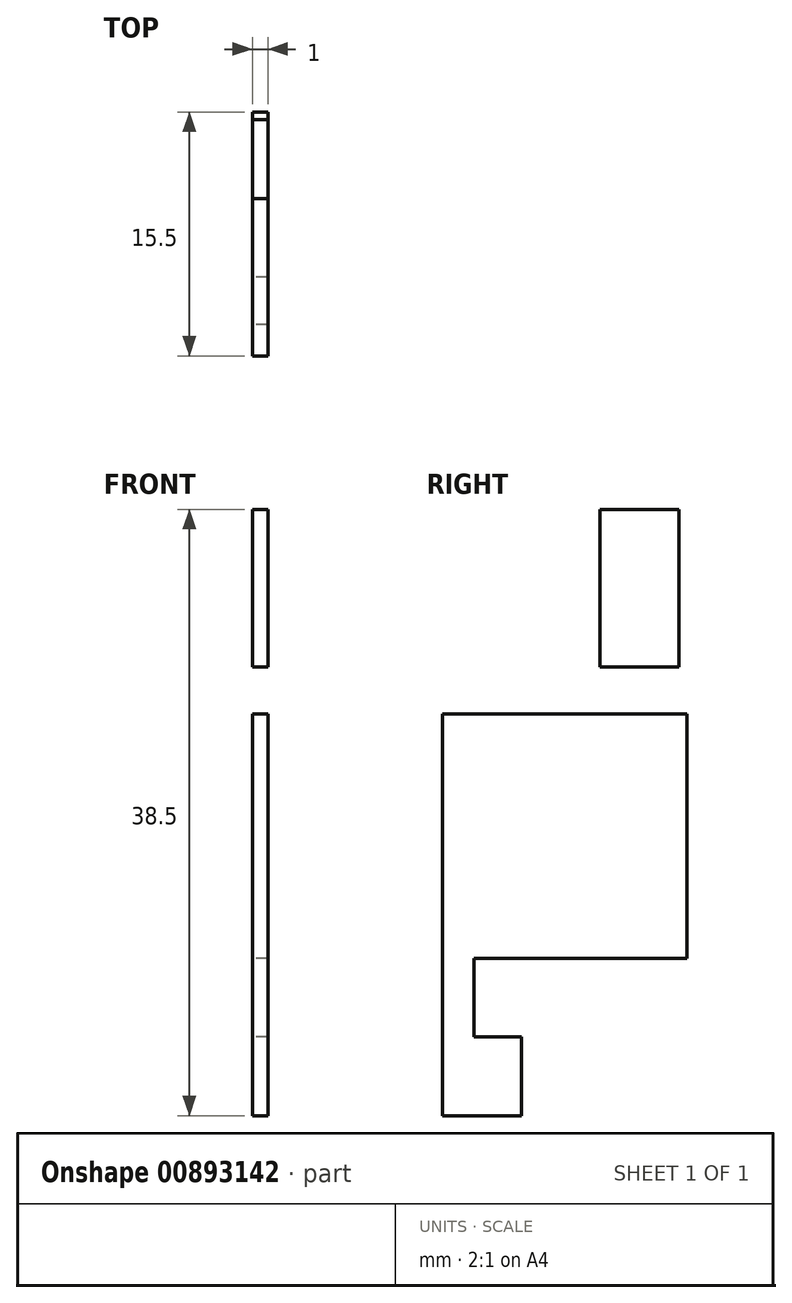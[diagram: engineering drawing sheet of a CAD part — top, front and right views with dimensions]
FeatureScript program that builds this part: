
annotation { "Feature Type Name" : "Feature", "Feature Type Description" : "" }
export const myFeature = defineFeature(function(context is Context, id is Id, definition is map)
    precondition{}
    {
        {
            var Q0;
            Q0=qCreatedBy(makeId("Right.planeOp"),FACE);
            var sketch = newSketch(context, id + "F0", { "sketchPlane" : qUnion([Q0])});
            skLineSegment(sketch, "E0.bottom", {"start": v(0, 0) * mm, "end": v(11.5, 0) * mm});
            skLineSegment(sketch, "E0.top", {"start": v(0, -15) * mm, "end": v(4.35, -15) * mm});
            skLineSegment(sketch, "E1.trimOffspring", {"start": v(7.15, -15) * mm, "end": v(11.5, -15) * mm});
            skLineSegment(sketch, "E2", {"start": v(12.38, 18) * mm, "end": v(9.14, 18) * mm});
            skLineSegment(sketch, "E3.0", {"start": v(-1.75, 0) * mm, "end": v(-1.75, -15) * mm});
            skLineSegment(sketch, "E4.0", {"start": v(13.25, 0) * mm, "end": v(13.25, -15) * mm});
            skLineSegment(sketch, "E5", {"start": v(-1.75, 0) * mm, "end": v(13.25, 0) * mm});
            skLineSegment(sketch, "E6", {"start": v(13.25, -15) * mm, "end": v(7.15, -15) * mm});
            skPoint(sketch, "E7.orphan", {"position": v(7.38, 18) * mm});
            skPoint(sketch, "E8.orphan", {"position": v(7.38, 3) * mm});
            skLineSegment(sketch, "E9", {"start": v(13.57, 18) * mm, "end": v(9.14, 18) * mm});
            skPoint(sketch, "E10.start.orphan", {"position": v(5.75, -15) * mm});
            skLineSegment(sketch, "E11", {"start": v(7.87, 18) * mm, "end": v(9.14, 18) * mm});
            skLineSegment(sketch, "E12", {"start": v(7.88, 13) * mm, "end": v(10.98, 13) * mm});
            skLineSegment(sketch, "E13.0", {"start": v(-3.75, 0) * mm, "end": v(-3.75, -15) * mm});
            skLineSegment(sketch, "E14.0", {"start": v(15.25, 0) * mm, "end": v(15.25, -15) * mm});
            skLineSegment(sketch, "E15", {"start": v(-2, 0) * mm, "end": v(13.5, 0) * mm});
            skLineSegment(sketch, "E16", {"start": v(-3.75, -15) * mm, "end": v(15.25, -15) * mm});
            skLineSegment(sketch, "E17.0", {"start": v(-3.75, -15.5) * mm, "end": v(15.25, -15.5) * mm});
            skLineSegment(sketch, "E18.0", {"start": v(-2, 0) * mm, "end": v(-2, -15) * mm});
            skLineSegment(sketch, "E19.0", {"start": v(13.5, 0) * mm, "end": v(13.5, -15) * mm});
            skLineSegment(sketch, "E20", {"start": v(-2, -15) * mm, "end": v(-2, -15.5) * mm});
            skLineSegment(sketch, "E21", {"start": v(13.5, -15) * mm, "end": v(13.5, -15.5) * mm});
            skLineSegment(sketch, "E22", {"start": v(10.98, 13) * mm, "end": v(6.98, 13) * mm});
            skLineSegment(sketch, "E23", {"start": v(6.98, 3) * mm, "end": v(10.98, 3) * mm});
            skLineSegment(sketch, "E24", {"start": v(11.38, 13) * mm, "end": v(10.98, 13) * mm});
            skLineSegment(sketch, "E25", {"start": v(11.38, 3) * mm, "end": v(10.98, 3) * mm});
            skLineSegment(sketch, "E26", {"start": v(11.88, 13) * mm, "end": v(11.38, 13) * mm});
            skLineSegment(sketch, "E27", {"start": v(11.88, 3) * mm, "end": v(11.38, 3) * mm});
            skLineSegment(sketch, "E28", {"start": v(6.98, 3) * mm, "end": v(6.88, 3) * mm});
            skLineSegment(sketch, "E29", {"start": v(6.98, 13) * mm, "end": v(6.88, 13) * mm});
            skLineSegment(sketch, "E30.0", {"start": v(13, 13) * mm, "end": v(13, 3) * mm});
            skLineSegment(sketch, "E31.0", {"start": v(8, 3) * mm, "end": v(8, 13) * mm});
            skLineSegment(sketch, "E32", {"start": v(13, 13) * mm, "end": v(8, 13) * mm});
            skLineSegment(sketch, "E33", {"start": v(13, 3) * mm, "end": v(8, 3) * mm});
            skLineSegment(sketch, "E34", {"start": v(-2, -15.5) * mm, "end": v(-2, -25.5) * mm});
            skLineSegment(sketch, "E35", {"start": v(-2, -25.5) * mm, "end": v(3, -25.5) * mm});
            skLineSegment(sketch, "E36", {"start": v(3, -25.5) * mm, "end": v(3, -20.5) * mm});
            skLineSegment(sketch, "E37", {"start": v(3, -20.5) * mm, "end": v(0, -20.5) * mm});
            skLineSegment(sketch, "E38", {"start": v(0, -20.5) * mm, "end": v(0, -15.5) * mm});
            skSolve(sketch);
        }
        {
            var Q0;
            Q0=makeQuery(id+"F0.imprint","IMPRINT",FACE,{"disambiguationData":[TD([[makeQuery(id+"F0.imprint","IMPRINT",EDGE,{"derivedFrom":sQuery(id+"F0.wireOp",EDGE,"E0.bottom")}),-1.0]])]});
            var Q1;
            Q1=makeQuery(id+"F0.imprint","IMPRINT",FACE,{"disambiguationData":[TD([[makeQuery(id+"F0.imprint","IMPRINT",EDGE,{"derivedFrom":sQuery(id+"F0.wireOp",EDGE,"qPRy3xUT-NRqM-xTn5-TbLo-p4iQvefC5ACk")}),-1.0]])]});
            var Q2;
            {var subQ3=sQuery(id+"F0.wireOp",EDGE,"63f1d356-c40f-4f39-ade3-4e022c9102be.0");Q2=makeQuery(id+"F0.imprint","IMPRINT",FACE,{"disambiguationData":[TD([[makeQuery(id+"F0.imprint","IMPRINT",EDGE,{"derivedFrom":subQ3}),1.0]])]});}
            var Q3;
            {var subQ0=sQuery(id+"F0.wireOp",EDGE,"5dc07093-3f57-4306-a93b-4e72212c7467.0");Q3=makeQuery(id+"F0.imprint","IMPRINT",FACE,{"disambiguationData":[TD([[makeQuery(id+"F0.imprint","IMPRINT",EDGE,{"derivedFrom":subQ0}),1.0]])]});}
            var Q4;
            {var subQ0=sQuery(id+"F0.wireOp",EDGE,"51NmYdBp-mA1z-wu9Q-53MT-rEDAkP0LJ8wn");Q4=makeQuery(id+"F0.imprint","IMPRINT",FACE,{"disambiguationData":[TD([[makeQuery(id+"F0.imprint","IMPRINT",EDGE,{"derivedFrom":subQ0}),-1.0]])]});}
            var Q5;
            {var subQ0=sQuery(id+"F0.wireOp",EDGE,"gVsyd78I-1lBY-GYfF-3Sc2-CoKCdImTYK3s");Q5=makeQuery(id+"F0.imprint","IMPRINT",FACE,{"disambiguationData":[TD([[makeQuery(id+"F0.imprint","IMPRINT",EDGE,{"derivedFrom":subQ0}),-1.0]])]});}
            var Q6;
            {var subQ3=sQuery(id+"F0.wireOp",EDGE,"SiENeyCx-ZrQ5-kKsV-lLu2-aJ1GO4VE4cTd");Q6=makeQuery(id+"F0.imprint","IMPRINT",FACE,{"disambiguationData":[TD([[makeQuery(id+"F0.imprint","IMPRINT",EDGE,{"derivedFrom":subQ3}),1.0]])]});}
            var Q7;
            {var subQ0=sQuery(id+"F0.wireOp",EDGE,"E3.0");Q7=makeQuery(id+"F0.imprint","IMPRINT",FACE,{"disambiguationData":[TD([[makeQuery(id+"F0.imprint","IMPRINT",EDGE,{"derivedFrom":subQ0}),-1.0]])]});}
            var Q8;
            {var subQ0=sQuery(id+"F0.wireOp",EDGE,"E4.0");Q8=makeQuery(id+"F0.imprint","IMPRINT",FACE,{"disambiguationData":[TD([[makeQuery(id+"F0.imprint","IMPRINT",EDGE,{"derivedFrom":subQ0}),1.0]])]});}
            var Q9;
            {var subQ2=sQuery(id+"F0.wireOp",EDGE,"1mKygX2L-qfZs-mII2-diun-zsKhjgC72kff");Q9=makeQuery(id+"F0.imprint","IMPRINT",FACE,{"disambiguationData":[TD([[makeQuery(id+"F0.imprint","IMPRINT",EDGE,{"derivedFrom":subQ2}),-1.0]])]});}
            var Q10;
            {var subQ0=sQuery(id+"F0.wireOp",EDGE,"zi8WKg8l-IywR-yDlg-Gw4f-iAsSbMJXHt8X");var subQ3=makeQuery(id+"F0.imprint","IMPRINT",VERTEX,{"disambiguationData":[OD(0.0)],"derivedFrom":subQ0});Q10=makeQuery(id+"F0.imprint","IMPRINT",FACE,{"disambiguationData":[TD([[makeQuery(id+"F0.imprint","IMPRINT",EDGE,{"disambiguationData":[TD([[subQ3,-1.0]])],"derivedFrom":subQ0}),1.0]])]});}
            var Q11;
            {var subQ0=sQuery(id+"F0.wireOp",EDGE,"E16");var subQ1=sQuery(id+"F0.wireOp",EDGE,"9c8eaf94-47ad-4e4a-b23c-c071626e9017.0");var subQ2=makeQuery(id+"F0.imprint","INTERSECT",VERTEX,{"derivedFrom":[subQ1,subQ0]});Q11=makeQuery(id+"F0.imprint","IMPRINT",FACE,{"disambiguationData":[TD([[makeQuery(id+"F0.imprint","IMPRINT",EDGE,{"disambiguationData":[TD([[subQ2,-1.0]])],"derivedFrom":subQ1}),1.0]])]});}
            var Q12;
            Q12=makeQuery(id+"F0.imprint","IMPRINT",FACE,{"disambiguationData":[TD([[makeQuery(id+"F0.imprint","IMPRINT",EDGE,{"derivedFrom":sQuery(id+"F0.wireOp",EDGE,"b8907b82-ca3a-4fe0-9ae4-8b5bafafc062.0")}),1.0]])]});
            var Q13;
            {var subQ3=sQuery(id+"F0.wireOp",EDGE,"E3.0");Q13=makeQuery(id+"F0.imprint","IMPRINT",FACE,{"disambiguationData":[TD([[makeQuery(id+"F0.imprint","IMPRINT",EDGE,{"derivedFrom":subQ3}),1.0]])]});}
            var Q14;
            {var subQ5=sQuery(id+"F0.wireOp",EDGE,"3820a88b-3abb-40db-8bfc-c48b148b7aa2.0");Q14=makeQuery(id+"F0.imprint","IMPRINT",FACE,{"disambiguationData":[TD([[makeQuery(id+"F0.imprint","IMPRINT",EDGE,{"derivedFrom":subQ5}),-1.0]])]});}
            var Q15;
            {var subQ0=sQuery(id+"F0.wireOp",EDGE,"e7f2dfaa-ca02-423d-a241-3264b2101ff0.0");Q15=makeQuery(id+"F0.imprint","IMPRINT",FACE,{"disambiguationData":[TD([[makeQuery(id+"F0.imprint","IMPRINT",EDGE,{"derivedFrom":subQ0}),1.0]])]});}
            var Q16;
            {var subQ0=sQuery(id+"F0.wireOp",EDGE,"f3faf3d2-6f8b-4572-bc8f-cff6e40356fd.0");var subQ1=sQuery(id+"F0.wireOp",EDGE,"9c8eaf94-47ad-4e4a-b23c-c071626e9017.0");var subQ2=makeQuery(id+"F0.imprint","INTERSECT",VERTEX,{"derivedFrom":[subQ1,subQ0]});Q16=makeQuery(id+"F0.imprint","IMPRINT",FACE,{"disambiguationData":[TD([[makeQuery(id+"F0.imprint","IMPRINT",EDGE,{"disambiguationData":[TD([[subQ2,1.0]])],"derivedFrom":subQ1}),1.0]])]});}
            var Q17;
            {var subQ7=sQuery(id+"F0.wireOp",EDGE,"E20");Q17=makeQuery(id+"F0.imprint","IMPRINT",FACE,{"disambiguationData":[TD([[makeQuery(id+"F0.imprint","IMPRINT",EDGE,{"derivedFrom":subQ7}),1.0]])]});}
            var Q18;
            {var subQ2=sQuery(id+"F0.wireOp",EDGE,"E21");Q18=makeQuery(id+"F0.imprint","IMPRINT",FACE,{"disambiguationData":[TD([[makeQuery(id+"F0.imprint","IMPRINT",EDGE,{"derivedFrom":subQ2}),-1.0]])]});}
            var Q19;
            {var subQ0=sQuery(id+"F0.wireOp",EDGE,"e1832ce9-9692-4c92-918f-52eea242351d.0");Q19=makeQuery(id+"F0.imprint","IMPRINT",FACE,{"disambiguationData":[TD([[makeQuery(id+"F0.imprint","IMPRINT",EDGE,{"derivedFrom":subQ0}),-1.0]])]});}
            var Q20;
            {var subQ0=sQuery(id+"F0.wireOp",EDGE,"04c29579-a2e5-4540-a143-d3ab26432ee8.0");Q20=makeQuery(id+"F0.imprint","IMPRINT",FACE,{"disambiguationData":[TD([[makeQuery(id+"F0.imprint","IMPRINT",EDGE,{"derivedFrom":subQ0}),-1.0]])]});}
            var Q21;
            {var subQ0=sQuery(id+"F0.wireOp",EDGE,"c4b32359-1725-4305-a7d0-088cad5a7380.0");Q21=makeQuery(id+"F0.imprint","IMPRINT",FACE,{"disambiguationData":[TD([[makeQuery(id+"F0.imprint","IMPRINT",EDGE,{"derivedFrom":subQ0}),1.0]])]});}
            var Q22;
            {var subQ0=sQuery(id+"F0.wireOp",EDGE,"04c29579-a2e5-4540-a143-d3ab26432ee8.0");Q22=makeQuery(id+"F0.imprint","IMPRINT",FACE,{"disambiguationData":[TD([[makeQuery(id+"F0.imprint","IMPRINT",EDGE,{"derivedFrom":subQ0}),1.0]])]});}
            var Q23;
            {var subQ5=sQuery(id+"F0.wireOp",EDGE,"a76b719a-5e5b-4d65-aa66-56cd854adb41.trimOffspring");Q23=makeQuery(id+"F0.imprint","IMPRINT",FACE,{"disambiguationData":[TD([[makeQuery(id+"F0.imprint","IMPRINT",EDGE,{"derivedFrom":subQ5}),1.0]])]});}
            var Q24;
            {var subQ0=sQuery(id+"F0.wireOp",EDGE,"65d9d9e5-3152-4186-b4e5-152fd11331dc.0");var subQ1=sQuery(id+"F0.wireOp",EDGE,"E16");var subQ2=makeQuery(id+"F0.imprint","INTERSECT",VERTEX,{"derivedFrom":[subQ1,subQ0]});Q24=makeQuery(id+"F0.imprint","IMPRINT",FACE,{"disambiguationData":[TD([[makeQuery(id+"F0.imprint","IMPRINT",EDGE,{"disambiguationData":[TD([[subQ2,-1.0]])],"derivedFrom":subQ1}),-1.0]])]});}
            var Q25;
            {var subQ0=sQuery(id+"F0.wireOp",EDGE,"E16");var subQ1=sQuery(id+"F0.wireOp",EDGE,"4ce51b92-a383-4be4-83d4-884a6f0044ea.0");var subQ2=makeQuery(id+"F0.imprint","INTERSECT",VERTEX,{"derivedFrom":[subQ1,subQ0]});Q25=makeQuery(id+"F0.imprint","IMPRINT",FACE,{"disambiguationData":[TD([[makeQuery(id+"F0.imprint","IMPRINT",EDGE,{"disambiguationData":[TD([[subQ2,-1.0]])],"derivedFrom":subQ1}),-1.0]])]});}
            var Q26;
            {var subQ5=sQuery(id+"F0.wireOp",EDGE,"e7f2dfaa-ca02-423d-a241-3264b2101ff0.0");Q26=makeQuery(id+"F0.imprint","IMPRINT",FACE,{"disambiguationData":[TD([[makeQuery(id+"F0.imprint","IMPRINT",EDGE,{"derivedFrom":subQ5}),-1.0]])]});}
            var Q27;
            {var subQ0=sQuery(id+"F0.wireOp",EDGE,"a76b719a-5e5b-4d65-aa66-56cd854adb41.trimOffspring");Q27=makeQuery(id+"F0.imprint","IMPRINT",FACE,{"disambiguationData":[TD([[makeQuery(id+"F0.imprint","IMPRINT",EDGE,{"derivedFrom":subQ0}),-1.0]])]});}
            var Q28;
            {var subQ0=sQuery(id+"F0.wireOp",EDGE,"471e34d8-23d2-4a55-bd43-ceb2bf1c369c.0");var subQ1=sQuery(id+"F0.wireOp",EDGE,"E16");var subQ2=makeQuery(id+"F0.imprint","INTERSECT",VERTEX,{"derivedFrom":[subQ1,subQ0]});Q28=makeQuery(id+"F0.imprint","IMPRINT",FACE,{"disambiguationData":[TD([[makeQuery(id+"F0.imprint","IMPRINT",EDGE,{"disambiguationData":[TD([[subQ2,-1.0]])],"derivedFrom":subQ1}),-1.0]])]});}
            var Q29;
            Q29=makeQuery(id+"F0.imprint","IMPRINT",FACE,{"disambiguationData":[TD([[makeQuery(id+"F0.imprint","IMPRINT",EDGE,{"derivedFrom":sQuery(id+"F0.wireOp",EDGE,"1ca92b4e-f661-4329-9906-1ec775b7465d.0")}),1.0]])]});
            var Q30;
            {var subQ0=sQuery(id+"F0.wireOp",EDGE,"471e34d8-23d2-4a55-bd43-ceb2bf1c369c.0");var subQ1=sQuery(id+"F0.wireOp",EDGE,"E16");var subQ2=makeQuery(id+"F0.imprint","INTERSECT",VERTEX,{"derivedFrom":[subQ1,subQ0]});Q30=makeQuery(id+"F0.imprint","IMPRINT",FACE,{"disambiguationData":[TD([[makeQuery(id+"F0.imprint","IMPRINT",EDGE,{"disambiguationData":[TD([[subQ2,-1.0]])],"derivedFrom":subQ1}),-1.0]])]});}
            var Q31;
            Q31=makeQuery(id+"F0.imprint","IMPRINT",FACE,{"disambiguationData":[TD([[makeQuery(id+"F0.imprint","IMPRINT",EDGE,{"derivedFrom":sQuery(id+"F0.wireOp",EDGE,"E23")}),1.0]])]});
            var Q32;
            {var subQ3=sQuery(id+"F0.wireOp",EDGE,"E30.0");Q32=makeQuery(id+"F0.imprint","IMPRINT",FACE,{"disambiguationData":[TD([[makeQuery(id+"F0.imprint","IMPRINT",EDGE,{"derivedFrom":subQ3}),-1.0]])]});}
            var Q33;
            {var subQ0=sQuery(id+"F0.wireOp",EDGE,"E34");Q33=makeQuery(id+"F0.imprint","IMPRINT",FACE,{"disambiguationData":[TD([[makeQuery(id+"F0.imprint","IMPRINT",EDGE,{"derivedFrom":subQ0}),1.0]])]});}
            extrude(context, id + "F1", {"entities" : qUnion([Q0, Q1, Q2, Q3, Q4, Q5, Q6, Q7, Q8, Q9, Q10, Q11, Q12, Q13, Q14, Q15, Q16, Q17, Q18, Q19, Q20, Q21, Q22, Q23, Q24, Q25, Q26, Q27, Q28, Q29, Q30, Q31, Q32, Q33]), "depth" : 1 * mm, "offsetDistance" : 25 * mm});
        }
    });
